FCSTD DOCUMENT  (FreeCAD 1.0R39109 (Git))
Label: asm_roof
License: All rights reserved
LicenseURL: https://en.wikipedia.org/wiki/All_rights_reserved
objects: App::Link×20, App::FeaturePython×15, Assembly::AssemblyLink×2, Assembly::JointGroup×1, Assembly::AssemblyObject×1
EXTERNAL_REF file=../parts/plate_roof.FCStd obj=Body
EXTERNAL_REF file=../secondary/linear_slide.FCStd obj=Body
EXTERNAL_REF file=asm_cam_holder.FCStd obj=Assembly
EXTERNAL_REF file=asm_shf.FCStd obj=Assembly
EXTERNAL_REF file=asm_shf.FCStd obj=SHF12
EXTERNAL_REF file=asm_shf.FCStd obj=Hex_socket_head_cap_screw_DIN_912_M4_15_0
EXTERNAL_REF file=asm_shf.FCStd obj=Hex_socket_head_cap_screw_DIN_912_M5_15_0
EXTERNAL_REF file=asm_shf.FCStd obj=Hex_socket_head_cap_screw_DIN_912_M5_15_001
EXTERNAL_REF file=../secondary/nuts_hexagonal.FCStd obj=Part__Feature001
EXTERNAL_REF file=../secondary/nuts_hexagonal.FCStd obj=Part__Feature

FEATURE [App::Link] plate_roof001  label="plate_roof"
  LinkedObject = -> <external ../parts/plate_roof.FCStd>#Body
FEATURE [App::FeaturePython] GroundedJoint  # Assembly grounded joint (typed FeaturePython)
  ObjectToGround = -> plate_roof001
FEATURE [App::Link] linear_slide  label="linear_slide_12"
  LinkPlacement = pos=(-38,-53.8,-15.1359) rot=(0,0,1;0rad)
  LinkedObject = -> <external ../secondary/linear_slide.FCStd>#Body
  Placement = pos=(-38,-53.8,-15.1359) rot=(0,0,1;0rad)
FEATURE [App::Link] linear_slide001  label="linear_slide_12_001"
  LinkPlacement = pos=(38,-53.8,-15.136) rot=(0,0,1;0rad)
  LinkedObject = -> <external ../secondary/linear_slide.FCStd>#Body
  Placement = pos=(38,-53.8,-15.136) rot=(0,0,1;0rad)
FEATURE [App::Link] asm_cam_holder
  LinkPlacement = pos=(-1.51e-14,-53.8,66.8641) rot=(0,0,1;1.5708rad)
  LinkedObject = -> <external asm_cam_holder.FCStd>#Assembly
  Placement = pos=(-1.51e-14,-53.8,66.8641) rot=(0,0,1;1.5708rad)
FEATURE [App::Link] SHF12
  LinkedObject = -> <external asm_shf.FCStd>#SHF12
FEATURE [App::Link] Hex_socket_head_cap_screw_DIN_912_M4_15_0  label="Hex socket head cap screw DIN 912 M4 15.0"
  LinkPlacement = pos=(12.25,6.5,11.5) rot=(0,-1,0;1.5708rad)
  LinkedObject = -> <external asm_shf.FCStd>#Hex_socket_head_cap_screw_DIN_912_M4_15_0
  Placement = pos=(12.25,6.5,11.5) rot=(0,-1,0;1.5708rad)
FEATURE [App::Link] Hex_socket_head_cap_screw_DIN_912_M5_15_0  label="Hex socket head cap screw DIN 912 M5 15.0"
  LinkPlacement = pos=(18,11,1.16e-14) rot=(0.57735,-0.57735,0.57735;2.0944rad)
  LinkedObject = -> <external asm_shf.FCStd>#Hex_socket_head_cap_screw_DIN_912_M5_15_0
  Placement = pos=(18,11,1.16e-14) rot=(0.57735,-0.57735,0.57735;2.0944rad)
FEATURE [App::Link] Hex_socket_head_cap_screw_DIN_912_M5_15_001  label="Hex socket head cap screw DIN 912 M5 15.001"
  LinkPlacement = pos=(-18,11,1.16e-14) rot=(0.57735,-0.57735,0.57735;2.0944rad)
  LinkedObject = -> <external asm_shf.FCStd>#Hex_socket_head_cap_screw_DIN_912_M5_15_001
  Placement = pos=(-18,11,1.16e-14) rot=(0.57735,-0.57735,0.57735;2.0944rad)
FEATURE [Assembly::AssemblyLink] asm_SHF
  Group = -> [SHF12,Hex_socket_head_cap_screw_DIN_912_M4_15_0,Hex_socket_head_cap_screw_DIN_912_M5_15_0,Hex_socket_head_cap_screw_DIN_912_M5_15_001]
  LinkedObject = -> <external asm_shf.FCStd>#Assembly
  Origin = -> Origin001
  Placement = pos=(38,-53.8,0) rot=(0.57735,0.57735,-0.57735;4.18879rad)
  Rigid = true
FEATURE [App::Link] SHF013
  LinkedObject = -> <external asm_shf.FCStd>#SHF12
FEATURE [App::Link] Hex_socket_head_cap_screw_DIN_912_M4_15_001  label="Hex socket head cap screw DIN 912 M4 15.001"
  LinkPlacement = pos=(12.25,6.5,11.5) rot=(0,-1,0;1.5708rad)
  LinkedObject = -> <external asm_shf.FCStd>#Hex_socket_head_cap_screw_DIN_912_M4_15_0
  Placement = pos=(12.25,6.5,11.5) rot=(0,-1,0;1.5708rad)
FEATURE [App::Link] Hex_socket_head_cap_screw_DIN_912_M5_15_002  label="Hex socket head cap screw DIN 912 M5 15.002"
  LinkPlacement = pos=(18,11,1.16e-14) rot=(0.57735,-0.57735,0.57735;2.0944rad)
  LinkedObject = -> <external asm_shf.FCStd>#Hex_socket_head_cap_screw_DIN_912_M5_15_0
  Placement = pos=(18,11,1.16e-14) rot=(0.57735,-0.57735,0.57735;2.0944rad)
FEATURE [App::Link] Hex_socket_head_cap_screw_DIN_912_M5_15_003  label="Hex socket head cap screw DIN 912 M5 15.003"
  LinkPlacement = pos=(-18,11,1.16e-14) rot=(0.57735,-0.57735,0.57735;2.0944rad)
  LinkedObject = -> <external asm_shf.FCStd>#Hex_socket_head_cap_screw_DIN_912_M5_15_001
  Placement = pos=(-18,11,1.16e-14) rot=(0.57735,-0.57735,0.57735;2.0944rad)
FEATURE [Assembly::AssemblyLink] asm_SHF001
  Group = -> [SHF013,Hex_socket_head_cap_screw_DIN_912_M4_15_001,Hex_socket_head_cap_screw_DIN_912_M5_15_002,Hex_socket_head_cap_screw_DIN_912_M5_15_003]
  LinkedObject = -> <external asm_shf.FCStd>#Assembly
  Origin = -> Origin002
  Placement = pos=(-38,-53.8,0) rot=(0.57735,0.57735,-0.57735;4.18879rad)
  Rigid = true
FEATURE [App::FeaturePython] Joint  label="Fixed"  # Assembly joint (typed FeaturePython)
  Activated = true
  AngleMax = 0
  AngleMin = 0
  Detach1 = false
  Detach2 = false
  Distance = 0
  Distance2 = 0
  EnableAngleMax = false
  EnableAngleMin = false
  EnableLengthMax = false
  EnableLengthMin = false
  JointType = 0 (Fixed)
  LengthMax = 0
  LengthMin = 0
  Placement1 = pos=(18,0,1.16e-14) rot=(-0.57735,0.57735,0.57735;2.0944rad)
  Placement2 = pos=(38,-35.8,0) rot=(0,0,1;0rad)
  Reference1 = -> Assembly [asm_SHF.SHF12.Edge23,asm_SHF.SHF12.Edge23]
  Reference2 = -> Assembly [plate_roof001.Edge35,plate_roof001.Edge35]
FEATURE [App::FeaturePython] Joint001  label="Fixed001"  # Assembly joint (typed FeaturePython)
  Activated = true
  AngleMax = 0
  AngleMin = 0
  Detach1 = false
  Detach2 = false
  Distance = 0
  Distance2 = 0
  EnableAngleMax = false
  EnableAngleMin = false
  EnableLengthMax = false
  EnableLengthMin = false
  JointType = 0 (Fixed)
  LengthMax = 0
  LengthMin = 0
  Placement1 = pos=(18,0,1.16e-14) rot=(-0.57735,0.57735,0.57735;2.0944rad)
  Placement2 = pos=(-38,-35.8,0) rot=(0,0,1;0rad)
  Reference1 = -> Assembly [asm_SHF001.SHF013.Edge23,asm_SHF001.SHF013.Edge23]
  Reference2 = -> Assembly [plate_roof001.Edge41,plate_roof001.Edge41]
FEATURE [App::FeaturePython] Joint002  label="Slider"  # Assembly joint (typed FeaturePython)
  Activated = true
  AngleMax = 0
  AngleMin = 0
  Detach1 = false
  Detach2 = false
  Distance = 0
  Distance2 = 0
  EnableAngleMax = false
  EnableAngleMin = false
  EnableLengthMax = false
  EnableLengthMin = true
  JointType = 3 (Slider)
  LengthMax = 38.1914
  LengthMin = 2.13595
  Placement2 = pos=(0,13,0) rot=(-0.57735,-0.57735,0.57735;4.18879rad)
  Reference1 = -> Assembly [linear_slide001.Edge2,linear_slide001.Edge2]
  Reference2 = -> Assembly [asm_SHF.SHF12.Edge3,asm_SHF.SHF12.Edge3]
FEATURE [App::FeaturePython] Joint003  label="Slider001"  # Assembly joint (typed FeaturePython)
  Activated = true
  AngleMax = 0
  AngleMin = 0
  Detach1 = false
  Detach2 = false
  Distance = 0
  Distance2 = 0
  EnableAngleMax = false
  EnableAngleMin = false
  EnableLengthMax = false
  EnableLengthMin = false
  JointType = 3 (Slider)
  LengthMax = 0
  LengthMin = 0
  Placement2 = pos=(0,13,0) rot=(-0.57735,-0.57735,0.57735;4.18879rad)
  Reference1 = -> Assembly [linear_slide.Edge2,linear_slide.Edge2]
  Reference2 = -> Assembly [asm_SHF001.SHF013.Edge3,asm_SHF001.SHF013.Edge3]
FEATURE [App::FeaturePython] Joint004  label="Fixed002"  # Assembly joint (typed FeaturePython)
  Activated = true
  AngleMax = 0
  AngleMin = 0
  Detach1 = false
  Detach2 = false
  Distance = 0
  Distance2 = 0
  EnableAngleMax = false
  EnableAngleMin = false
  EnableLengthMax = false
  EnableLengthMin = false
  JointType = 0 (Fixed)
  LengthMax = 0
  LengthMin = 0
  Offset2 = pos=(0,0,0) rot=(0,0,1;3.14159rad)
  Placement1 = pos=(0,13,0) rot=(-0.57735,-0.57735,0.57735;4.18879rad)
  Placement2 = pos=(0,0,100) rot=(0,0,1;3.14159rad)
  Reference1 = -> Assembly [asm_cam_holder.asm_SHF001.SHF013.Edge3,asm_cam_holder.asm_SHF001.SHF013.Edge3]
  Reference2 = -> Assembly [linear_slide001.Edge3,linear_slide001.Edge3]
FEATURE [App::FeaturePython] Joint005  label="Fixed003"  # Assembly joint (typed FeaturePython)
  Activated = true
  AngleMax = 0
  AngleMin = 0
  Detach1 = false
  Detach2 = false
  Distance = 0
  Distance2 = 0
  EnableAngleMax = false
  EnableAngleMin = false
  EnableLengthMax = false
  EnableLengthMin = false
  JointType = 0 (Fixed)
  LengthMax = 0
  LengthMin = 0
  Placement1 = pos=(0,0,100) rot=(0,0,1;0rad)
  Placement2 = pos=(0,13,0) rot=(-0.57735,-0.57735,0.57735;4.18879rad)
  Reference1 = -> Assembly [linear_slide.Edge3,linear_slide.Edge3]
  Reference2 = -> Assembly [asm_cam_holder.asm_SHF.SHF12.Edge3,asm_cam_holder.asm_SHF.SHF12.Edge3]
FEATURE [App::Link] Hexagonal_Nut_M5_CBALN5  label="Hexagonal Nut M5_CBALN5"
  LinkPlacement = pos=(-38,-71.8,66.8641) rot=(0,1,0;4.71239rad)
  LinkedObject = -> <external ../secondary/nuts_hexagonal.FCStd>#Part__Feature001
  Placement = pos=(-38,-71.8,66.8641) rot=(0,1,0;4.71239rad)
FEATURE [App::Link] Hexagonal_Nut_M5_CBALN006  label="Hexagonal Nut M5_CBALN006"
  LinkPlacement = pos=(38,-71.8,66.864) rot=(0.707107,0,0.707107;3.14159rad)
  LinkedObject = -> <external ../secondary/nuts_hexagonal.FCStd>#Part__Feature001
  Placement = pos=(38,-71.8,66.864) rot=(0.707107,0,0.707107;3.14159rad)
FEATURE [App::Link] Hexagonal_Nut_M5_CBALN007  label="Hexagonal Nut M5_CBALN007"
  LinkPlacement = pos=(-38,-35.8,66.8641) rot=(0,-1,0;1.5708rad)
  LinkedObject = -> <external ../secondary/nuts_hexagonal.FCStd>#Part__Feature001
  Placement = pos=(-38,-35.8,66.8641) rot=(0,-1,0;1.5708rad)
FEATURE [App::Link] Hexagonal_Nut_M5_CBALN008  label="Hexagonal Nut M5_CBALN008"
  LinkPlacement = pos=(38,-35.8,66.864) rot=(0.707107,0,0.707107;3.14159rad)
  LinkedObject = -> <external ../secondary/nuts_hexagonal.FCStd>#Part__Feature001
  Placement = pos=(38,-35.8,66.864) rot=(0.707107,0,0.707107;3.14159rad)
FEATURE [App::FeaturePython] Joint006  label="Fixed004"  # Assembly joint (typed FeaturePython)
  Activated = true
  AngleMax = 0
  AngleMin = 0
  Detach1 = false
  Detach2 = false
  Distance = 0
  Distance2 = 0
  EnableAngleMax = false
  EnableAngleMin = false
  EnableLengthMax = false
  EnableLengthMin = false
  JointType = 0 (Fixed)
  LengthMax = 0
  LengthMin = 0
  Offset2 = pos=(0,0,-11) rot=(0,0,1;0rad)
  Placement1 = pos=(0,0,0) rot=(0,-1,0;1.5708rad)
  Placement2 = pos=(-1.8e-15,-7e-15,16) rot=(0,0,1;0rad)
  Reference1 = -> Assembly [Hexagonal_Nut_M5_CBALN008.Edge48,Hexagonal_Nut_M5_CBALN008.Edge48]
  Reference2 = -> Assembly [asm_cam_holder.asm_SHF001.Hex_socket_head_cap_screw_DIN_912_M5_15_002.Edge11,asm_cam_holder.asm_SHF001.Hex_socket_head_cap_screw_DIN_912_M5_15_002.Edge11]
FEATURE [App::FeaturePython] Joint007  label="Fixed005"  # Assembly joint (typed FeaturePython)
  Activated = true
  AngleMax = 0
  AngleMin = 0
  Detach1 = false
  Detach2 = false
  Distance = 0
  Distance2 = 0
  EnableAngleMax = false
  EnableAngleMin = false
  EnableLengthMax = false
  EnableLengthMin = false
  JointType = 0 (Fixed)
  LengthMax = 0
  LengthMin = 0
  Offset2 = pos=(0,0,-11) rot=(0,0,1;0rad)
  Placement1 = pos=(0,0,0) rot=(0,-1,0;1.5708rad)
  Placement2 = pos=(0,-3.6e-15,16) rot=(0,0,1;0rad)
  Reference1 = -> Assembly [Hexagonal_Nut_M5_CBALN006.Edge28,Hexagonal_Nut_M5_CBALN006.Edge28]
  Reference2 = -> Assembly [asm_cam_holder.asm_SHF001.Hex_socket_head_cap_screw_DIN_912_M5_15_003.Edge11,asm_cam_holder.asm_SHF001.Hex_socket_head_cap_screw_DIN_912_M5_15_003.Edge11]
FEATURE [App::FeaturePython] Joint008  label="Fixed006"  # Assembly joint (typed FeaturePython)
  Activated = true
  AngleMax = 0
  AngleMin = 0
  Detach1 = false
  Detach2 = false
  Distance = 0
  Distance2 = 0
  EnableAngleMax = false
  EnableAngleMin = false
  EnableLengthMax = false
  EnableLengthMin = false
  JointType = 0 (Fixed)
  LengthMax = 0
  LengthMin = 0
  Offset2 = pos=(0,0,-11) rot=(0,0,1;0rad)
  Placement1 = pos=(0,0,0) rot=(0,1,0;4.71239rad)
  Placement2 = pos=(0,-3.6e-15,16) rot=(0,0,1;0rad)
  Reference1 = -> Assembly [Hexagonal_Nut_M5_CBALN007.Edge28,Hexagonal_Nut_M5_CBALN007.Edge28]
  Reference2 = -> Assembly [asm_cam_holder.asm_SHF.Hex_socket_head_cap_screw_DIN_912_M5_15_001.Edge11,asm_cam_holder.asm_SHF.Hex_socket_head_cap_screw_DIN_912_M5_15_001.Edge11]
FEATURE [App::FeaturePython] Joint009  label="Fixed007"  # Assembly joint (typed FeaturePython)
  Activated = true
  AngleMax = 0
  AngleMin = 0
  Detach1 = false
  Detach2 = false
  Distance = 0
  Distance2 = 0
  EnableAngleMax = false
  EnableAngleMin = false
  EnableLengthMax = false
  EnableLengthMin = false
  JointType = 0 (Fixed)
  LengthMax = 0
  LengthMin = 0
  Offset2 = pos=(0,0,-11) rot=(0,0,1;0rad)
  Placement1 = pos=(0,0,0) rot=(0,-1,0;1.5708rad)
  Placement2 = pos=(-1.8e-15,-7e-15,16) rot=(0,0,1;0rad)
  Reference1 = -> Assembly [Hexagonal_Nut_M5_CBALN5.Edge28,Hexagonal_Nut_M5_CBALN5.Edge28]
  Reference2 = -> Assembly [asm_cam_holder.asm_SHF.Hex_socket_head_cap_screw_DIN_912_M5_15_0.Edge11,asm_cam_holder.asm_SHF.Hex_socket_head_cap_screw_DIN_912_M5_15_0.Edge11]
FEATURE [App::Link] Hexagonal_Nut_M4_CBALN4  label="Hexagonal Nut M4_CBALN4"
  LinkPlacement = pos=(32.96,-17.7689,66.8641) rot=(0.707107,0,0.707107;3.14159rad)
  LinkedObject = -> <external ../secondary/nuts_hexagonal.FCStd>#Part__Feature
  Placement = pos=(32.96,-17.7689,66.8641) rot=(0.707107,0,0.707107;3.14159rad)
FEATURE [App::Link] Hexagonal_Nut_M4_CBALN005  label="Hexagonal Nut M4_CBALN005"
  LinkPlacement = pos=(-32.96,-17.7689,66.8641) rot=(0.707107,0,0.707107;3.14159rad)
  LinkedObject = -> <external ../secondary/nuts_hexagonal.FCStd>#Part__Feature
  Placement = pos=(-32.96,-17.7689,66.8641) rot=(0.707107,0,0.707107;3.14159rad)
FEATURE [App::Link] Hexagonal_Nut_M4_CBALN006  label="Hexagonal Nut M4_CBALN006"
  LinkPlacement = pos=(-32.96,20.2311,66.8641) rot=(0.707107,0,0.707107;3.14159rad)
  LinkedObject = -> <external ../secondary/nuts_hexagonal.FCStd>#Part__Feature
  Placement = pos=(-32.96,20.2311,66.8641) rot=(0.707107,0,0.707107;3.14159rad)
FEATURE [App::Link] Hexagonal_Nut_M4_CBALN007  label="Hexagonal Nut M4_CBALN007"
  LinkPlacement = pos=(32.96,20.2311,66.864) rot=(0.707107,0,0.707107;3.14159rad)
  LinkedObject = -> <external ../secondary/nuts_hexagonal.FCStd>#Part__Feature
  Placement = pos=(32.96,20.2311,66.864) rot=(0.707107,0,0.707107;3.14159rad)
FEATURE [App::FeaturePython] Joint010  label="Fixed008"  # Assembly joint (typed FeaturePython)
  Activated = true
  AngleMax = 0
  AngleMin = 0
  Detach1 = false
  Detach2 = false
  Distance = 0
  Distance2 = 0
  EnableAngleMax = false
  EnableAngleMin = false
  EnableLengthMax = false
  EnableLengthMin = false
  JointType = 0 (Fixed)
  LengthMax = 0
  LengthMin = 0
  Offset2 = pos=(0,0,3) rot=(0,0,1;0rad)
  Placement1 = pos=(0,0,0) rot=(0,-1,0;1.5708rad)
  Placement2 = pos=(-6.98683,35.5575,3) rot=(0,0,1;0rad)
  Reference1 = -> Assembly [Hexagonal_Nut_M4_CBALN007.Edge31,Hexagonal_Nut_M4_CBALN007.Edge31]
  Reference2 = -> Assembly [asm_cam_holder.asm_cam_mount.Hex_screw_M4_10_003.Edge2,asm_cam_holder.asm_cam_mount.Hex_screw_M4_10_003.Edge2]
FEATURE [App::FeaturePython] Joint011  label="Fixed009"  # Assembly joint (typed FeaturePython)
  Activated = true
  AngleMax = 0
  AngleMin = 0
  Detach1 = false
  Detach2 = false
  Distance = 0
  Distance2 = 0
  EnableAngleMax = false
  EnableAngleMin = false
  EnableLengthMax = false
  EnableLengthMin = false
  JointType = 0 (Fixed)
  LengthMax = 0
  LengthMin = 0
  Offset2 = pos=(0,0,3) rot=(0,0,1;0rad)
  Placement1 = pos=(0,0,0) rot=(0,-1,0;1.5708rad)
  Placement2 = pos=(-6.98683,35.5575,3) rot=(0,0,1;0rad)
  Reference1 = -> Assembly [Hexagonal_Nut_M4_CBALN006.Edge31,Hexagonal_Nut_M4_CBALN006.Edge31]
  Reference2 = -> Assembly [asm_cam_holder.asm_cam_mount.Hex_screw_M4_10_001.Edge2,asm_cam_holder.asm_cam_mount.Hex_screw_M4_10_001.Edge2]
FEATURE [App::FeaturePython] Joint012  label="Fixed010"  # Assembly joint (typed FeaturePython)
  Activated = true
  AngleMax = 0
  AngleMin = 0
  Detach1 = false
  Detach2 = false
  Distance = 0
  Distance2 = 0
  EnableAngleMax = false
  EnableAngleMin = false
  EnableLengthMax = false
  EnableLengthMin = false
  JointType = 0 (Fixed)
  LengthMax = 0
  LengthMin = 0
  Offset2 = pos=(0,0,3) rot=(0,0,1;0rad)
  Placement1 = pos=(0,0,0) rot=(0,-1,0;1.5708rad)
  Placement2 = pos=(-6.98683,35.5575,3) rot=(0,0,1;0rad)
  Reference1 = -> Assembly [Hexagonal_Nut_M4_CBALN005.Edge31,Hexagonal_Nut_M4_CBALN005.Edge31]
  Reference2 = -> Assembly [asm_cam_holder.asm_cam_mount.Hex_screw_M4_10_0.Edge2,asm_cam_holder.asm_cam_mount.Hex_screw_M4_10_0.Edge2]
FEATURE [App::FeaturePython] Joint013  label="Fixed011"  # Assembly joint (typed FeaturePython)
  Activated = true
  AngleMax = 0
  AngleMin = 0
  Detach1 = false
  Detach2 = false
  Distance = 0
  Distance2 = 0
  EnableAngleMax = false
  EnableAngleMin = false
  EnableLengthMax = false
  EnableLengthMin = false
  JointType = 0 (Fixed)
  LengthMax = 0
  LengthMin = 0
  Offset2 = pos=(0,0,3) rot=(0,0,1;0rad)
  Placement1 = pos=(0,0,0) rot=(0,-1,0;1.5708rad)
  Placement2 = pos=(-6.98683,35.5575,3) rot=(0,0,1;0rad)
  Reference1 = -> Assembly [Hexagonal_Nut_M4_CBALN4.Edge31,Hexagonal_Nut_M4_CBALN4.Edge31]
  Reference2 = -> Assembly [asm_cam_holder.asm_cam_mount.Hex_screw_M4_10_002.Edge2,asm_cam_holder.asm_cam_mount.Hex_screw_M4_10_002.Edge2]
FEATURE [Assembly::JointGroup] Joints
  Group = -> [GroundedJoint,Joint,Joint001,Joint002,Joint003,Joint004,Joint005,Joint006,Joint007,Joint008,Joint009,Joint010,Joint011,Joint012,Joint013]
FEATURE [Assembly::AssemblyObject] Assembly  label="asm_roof"
  Group = -> [Joints,plate_roof001,GroundedJoint,linear_slide,linear_slide001,asm_cam_holder,asm_SHF,asm_SHF001,Joint,Joint001,Joint002,Joint003,Joint004,Joint005,Hexagonal_Nut_M5_CBALN5,Hexagonal_Nut_M5_CBALN006,Hexagonal_Nut_M5_CBALN007,Hexagonal_Nut_M5_CBALN008,Joint006,Joint007,Joint008,Joint009,Hexagonal_Nut_M4_CBALN4,Hexagonal_Nut_M4_CBALN005,Hexagonal_Nut_M4_CBALN006,Hexagonal_Nut_M4_CBALN007,Joint010,+3 more]
  Origin = -> Origin
  Type = Assembly

RESOLVED EXTERNAL PARTS (link-assembly join: the EXTERNAL_REF files above that resolve inside this repo's crawl, each included once):
---- part ../parts/plate_roof.FCStd = doc fcstd_1de5e0d9f138 ----
FCSTD DOCUMENT  (FreeCAD 1.0R38641 +468 (Git))
Label: plate_roof
License: All rights reserved
LicenseURL: https://en.wikipedia.org/wiki/All_rights_reserved
objects: TechDraw::DrawViewDimension×10, TechDraw::DrawProjGroupItem×2, Sketcher::SketchObject×1, PartDesign::Pad×1, PartDesign::Body×1, TechDraw::DrawSVGTemplate×1, TechDraw::DrawProjGroup×1, TechDraw::DrawPage×1
note: 22 computed .brp shape members not serialized (recipe doc carries the construction recipe); baked Part::Feature solids carry a one-line shape summary decoded from their .brp

FEATURE [Sketcher::SketchObject] Sketch
  ArcFitTolerance = 1e-06
  AttachmentSupport = -> [XY_Plane]
  FullyConstrained = false
  MakeInternals = false
  MapMode = 5
  sketch-geometry (16):
    g0: LineSegment StartX=-100 StartY=200 StartZ=0 EndX=-100 EndY=-200 EndZ=0
    g1: LineSegment StartX=-100 StartY=-200 StartZ=0 EndX=100 EndY=-200 EndZ=0
    g2: LineSegment StartX=100 StartY=-200 StartZ=0 EndX=100 EndY=200 EndZ=0
    g3: LineSegment StartX=100 StartY=200 StartZ=0 EndX=-100 EndY=200 EndZ=0
    g4: Circle CenterX=-44 CenterY=50.2 CenterZ=0 NormalX=0 NormalY=0 NormalZ=1 AngleXU=0 Radius=2.45
    g5: Circle CenterX=-44 CenterY=-157.8 CenterZ=0 NormalX=0 NormalY=0 NormalZ=1 AngleXU=0 Radius=2.45
    g6: Circle CenterX=44 CenterY=50.2 CenterZ=0 NormalX=0 NormalY=0 NormalZ=1 AngleXU=0 Radius=2.45
    g7: Circle CenterX=44 CenterY=-157.8 CenterZ=0 NormalX=0 NormalY=0 NormalZ=1 AngleXU=0 Radius=2.45
    g8: Circle [constr] CenterX=0 CenterY=0 CenterZ=0 NormalX=0 NormalY=0 NormalZ=1 AngleXU=0 Radius=9.44112
    g9: Circle CenterX=-38 CenterY=-35.8 CenterZ=0 NormalX=0 NormalY=0 NormalZ=1 AngleXU=0 Radius=1.95
    g10: Circle CenterX=-38 CenterY=-71.8 CenterZ=0 NormalX=0 NormalY=0 NormalZ=1 AngleXU=0 Radius=1.95
    g11: Circle CenterX=-38 CenterY=-53.8 CenterZ=0 NormalX=0 NormalY=0 NormalZ=1 AngleXU=0 Radius=6.5
    g12: Circle CenterX=38 CenterY=-35.8 CenterZ=0 NormalX=0 NormalY=0 NormalZ=1 AngleXU=0 Radius=1.95
    g13: Circle CenterX=38 CenterY=-53.8 CenterZ=0 NormalX=0 NormalY=0 NormalZ=1 AngleXU=0 Radius=6.5
    g14: Circle CenterX=38 CenterY=-71.8 CenterZ=0 NormalX=0 NormalY=0 NormalZ=1 AngleXU=0 Radius=1.95
    g15: LineSegment [constr] StartX=0 StartY=0 StartZ=0 EndX=0 EndY=174.663 EndZ=0
  constraints (44):
    c: Coincident(g0,g1)
    c: Coincident(g1,g2)
    c: Coincident(g2,g3)
    c: Coincident(g3,g0)
    c: Vertical(g0)
    c: Vertical(g2)
    c: Horizontal(g1)
    c: Horizontal(g3)
    c: DistanceY(g0,g0) = 400
    c: DistanceX(g3,g3) = 200
    c: Vertical(g4,g5)
    c: Diameter(g4) = 4.9
    c: Equal(g4,g5)
    c: DistanceY(g5,g4) = 208
    c: Horizontal(g6,g4)
    c: Horizontal(g7,g5)
    c: Equal(g6,g4)
    c: Equal(g4,g7)
    c: DistanceX(g4,g6) = 88
    c: Vertical(g7,g6)
    c: DistanceY(g8,g4) = 50.2
    c: DistanceX(g4,g8) = 44
    c: Distance(g8,g3) = 200
    c: Distance(g8,g0) = 100
    c: Vertical(g9,g11)
    c: Vertical(g11,g10)
    c: Vertical(g12,g13)
    c: Vertical(g13,g14)
    c: DistanceY(g11,g9) = 18
    c: DistanceY(g10,g11) = 18
    c: Diameter(g9) = 3.9
    c: Equal(g9,g10)
    c: Equal(g10,g12)
    c: Equal(g12,g14)
    c: Horizontal(g9,g12)
    c: Horizontal(g10,g14)
    c: Equal(g11,g13)
    c: Diameter(g11) = 13
    c: DistanceX(g11,g8) = 38
    c: Horizontal(g11,g13)
    c: DistanceY(g11,g4) = 104
    c: Coincident(g15,g8)
    c: Symmetric(g11,g13,g15)
    c: Coincident(g8,g-1)
FEATURE [PartDesign::Pad] Pad
  Direction = (0,0,1)
  Length = 3
  Length2 = 10
  Profile = -> Sketch
  ReferenceAxis = -> Sketch [N_Axis]
  Refine = true
  Suppressed = false
  Type = 0
FEATURE [PartDesign::Body] Body  label="plate_roof"
  AllowCompound = false
  Group = -> [Sketch,Pad]
  Origin = -> Origin
  Tip = -> Pad
FEATURE [TechDraw::DrawSVGTemplate] Template
  EditableTexts = approval_person=B. Hecate; creator=Djordje Vujic; date_of_issue=20.1.25.; document_type=Assembly Drawing; general_tolerances=ISO 2768-m; identification_number=DN; language_code=EN; part_material=Stainless steel Mat.No. 1.4301; revision_index=AAA; sheet_number=1 / 3; sheet_scale=1 : 2; title=plate_roof
  Height = 297
  Orientation = 0
  Template = /snap/freecad/1248/usr/share/Mod/TechDraw/Templates/A4_Portrait_ISO5457_minimal.svg
  Width = 210
FEATURE [TechDraw::DrawProjGroupItem] ProjItem  label="Front"
  CoarseView = false
  Direction = (0,0,1)
  Focus = 100
  HardHidden = false
  IsoCount = 0
  IsoHidden = false
  IsoVisible = false
  LockPosition = true
  Perspective = false
  Rotation = 0
  RotationVector = (1,0,0)
  Scale = 0.5
  ScaleType = 0
  ScrubCount = 1
  SeamHidden = false
  SeamVisible = false
  SmoothHidden = false
  SmoothVisible = true
  Source = -> [Body]
  Type = 0
  X = 0
  XDirection = (1,0,0)
  Y = 0
FEATURE [TechDraw::DrawProjGroupItem] ProjItem001  label="Bottom"
  CoarseView = false
  Direction = (0,-1,0)
  Focus = 100
  HardHidden = false
  IsoCount = 0
  IsoHidden = false
  IsoVisible = false
  LockPosition = false
  Perspective = false
  Rotation = 0
  RotationVector = (1,0,0)
  Scale = 0.5
  ScaleType = 0
  ScrubCount = 1
  SeamHidden = false
  SeamVisible = false
  SmoothHidden = false
  SmoothVisible = true
  Source = -> [Body]
  Type = 5
  X = 0
  XDirection = (1,0,0)
  Y = 115.75
FEATURE [TechDraw::DrawProjGroup] ProjGroup
  Anchor = -> ProjItem
  AutoDistribute = true
  LockPosition = false
  ProjectionType = 0
  Rotation = 0
  Scale = 0.5
  ScaleType = 2
  Source = -> [Body]
  Views = -> [ProjItem,ProjItem001]
  X = 105
  Y = 162.983
  spacingX = 15
  spacingY = 15
FEATURE [TechDraw::DrawViewDimension] Dimension
  AngleOverride = false
  Arbitrary = false
  ArbitraryTolerances = false
  BoxCorners = (2) [(-50,-0.75,0),(50,0.75,0)]
  EqualTolerance = true
  ExtensionAngle = 0
  FormatSpec = %.2w
  FormatSpecOverTolerance = %+.2w
  FormatSpecUnderTolerance = %+.2w
  Inverted = false
  LineAngle = 0
  LockPosition = false
  MeasureType = 1
  OverTolerance = 0
  References2D = -> [ProjItem001]
  Rotation = 0
  ScaleType = 0
  TheoreticalExact = false
  Type = 2
  UnderTolerance = 0
  X = -62.2509
  Y = -6.95305
FEATURE [TechDraw::DrawViewDimension] Dimension001
  AngleOverride = false
  Arbitrary = false
  ArbitraryTolerances = false
  BoxCorners = (2) [(-50,-0.75,0),(50,0.75,0)]
  EqualTolerance = true
  ExtensionAngle = 0
  FormatSpec = %.2w
  FormatSpecOverTolerance = %+.2w
  FormatSpecUnderTolerance = %+.2w
  Inverted = false
  LineAngle = 0
  LockPosition = false
  MeasureType = 1
  OverTolerance = 0
  References2D = -> [ProjItem001]
  Rotation = 0
  ScaleType = 0
  TheoreticalExact = false
  Type = 1
  UnderTolerance = 0
  X = 0
  Y = -5.41651
FEATURE [TechDraw::DrawViewDimension] Dimension002
  AngleOverride = false
  Arbitrary = false
  ArbitraryTolerances = false
  BoxCorners = (2) [(-50,-100,0),(50,100,0)]
  EqualTolerance = true
  ExtensionAngle = 0
  FormatSpec = %.2w
  FormatSpecOverTolerance = %+.2w
  FormatSpecUnderTolerance = %+.2w
  Inverted = false
  LineAngle = 0
  LockPosition = false
  MeasureType = 1
  OverTolerance = 0
  References2D = -> [ProjItem]
  Rotation = 0
  ScaleType = 0
  TheoreticalExact = false
  Type = 2
  UnderTolerance = 0
  X = -64.6458
  Y = 3.29053
FEATURE [TechDraw::DrawViewDimension] Dimension003
  AngleOverride = false
  Arbitrary = false
  ArbitraryTolerances = false
  BoxCorners = (2) [(-50,-100,0),(50,100,0)]
  EqualTolerance = true
  ExtensionAngle = 0
  FormatSpec = %.2w
  FormatSpecOverTolerance = %+.2w
  FormatSpecUnderTolerance = %+.2w
  Inverted = false
  LineAngle = 0
  LockPosition = false
  MeasureType = 1
  OverTolerance = 0
  References2D = -> [ProjItem]
  Rotation = 0
  ScaleType = 0
  TheoreticalExact = false
  Type = 0
  UnderTolerance = 0
  X = 29.0917
  Y = -31.4
FEATURE [TechDraw::DrawViewDimension] Dimension004
  AngleOverride = false
  Arbitrary = false
  ArbitraryTolerances = false
  BoxCorners = (2) [(-50,-100,0),(50,100,0)]
  EqualTolerance = true
  ExtensionAngle = 0
  FormatSpec = %.2w
  FormatSpecOverTolerance = %+.2w
  FormatSpecUnderTolerance = %+.2w
  Inverted = false
  LineAngle = 0
  LockPosition = false
  MeasureType = 1
  OverTolerance = 0
  References2D = -> [ProjItem]
  Rotation = 0
  ScaleType = 0
  TheoreticalExact = false
  Type = 0
  UnderTolerance = 0
  X = 0
  Y = -5.52183
FEATURE [TechDraw::DrawViewDimension] Dimension005
  AngleOverride = false
  Arbitrary = false
  ArbitraryTolerances = false
  BoxCorners = (2) [(-50,-100,0),(50,100,0)]
  EqualTolerance = true
  ExtensionAngle = 0
  FormatSpec = %.2w
  FormatSpecOverTolerance = %+.2w
  FormatSpecUnderTolerance = %+.2w
  Inverted = false
  LineAngle = 0
  LockPosition = false
  MeasureType = 1
  OverTolerance = 0
  References2D = -> [ProjItem]
  Rotation = 0
  ScaleType = 0
  TheoreticalExact = false
  Type = 0
  UnderTolerance = 0
  X = -34.5
  Y = -5.52183
FEATURE [TechDraw::DrawViewDimension] Dimension006
  AngleOverride = false
  Arbitrary = false
  ArbitraryTolerances = false
  BoxCorners = (2) [(-50,-100,0),(50,100,0)]
  EqualTolerance = true
  ExtensionAngle = 0
  FormatSpec = %.2w
  FormatSpecOverTolerance = %+.2w
  FormatSpecUnderTolerance = %+.2w
  Inverted = false
  LineAngle = 0
  LockPosition = false
  MeasureType = 1
  OverTolerance = 0
  References2D = -> [ProjItem]
  Rotation = 0
  ScaleType = 0
  TheoreticalExact = false
  Type = 0
  UnderTolerance = 0
  X = -33.0527
  Y = -22.4
FEATURE [TechDraw::DrawViewDimension] Dimension007
  AngleOverride = false
  Arbitrary = false
  ArbitraryTolerances = false
  BoxCorners = (2) [(-50,-100,0),(50,100,0)]
  EqualTolerance = false
  ExtensionAngle = 0
  FormatSpec = ⌀%.2w
  FormatSpecOverTolerance = %+.2w
  FormatSpecUnderTolerance = -%.2w
  Inverted = false
  LineAngle = 0
  LockPosition = false
  MeasureType = 1
  OverTolerance = 1
  References2D = -> [ProjItem]
  Rotation = 0
  ScaleType = 0
  TheoreticalExact = false
  Type = 5
  UnderTolerance = 0.9
  X = -9.88409
  Y = -19.3744
FEATURE [TechDraw::DrawViewDimension] Dimension008
  AngleOverride = false
  Arbitrary = false
  ArbitraryTolerances = false
  BoxCorners = (2) [(-50,-100,0),(50,100,0)]
  EqualTolerance = true
  ExtensionAngle = 0
  FormatSpec = %.2w
  FormatSpecOverTolerance = %+.2w
  FormatSpecUnderTolerance = %+.2w
  Inverted = false
  LineAngle = 0
  LockPosition = false
  MeasureType = 1
  OverTolerance = 1
  References2D = -> [ProjItem]
  Rotation = 0
  ScaleType = 0
  TheoreticalExact = false
  Type = 0
  UnderTolerance = -1
  X = 9.62605
  Y = -67.95
FEATURE [TechDraw::DrawViewDimension] Dimension009
  AngleOverride = false
  Arbitrary = false
  ArbitraryTolerances = false
  BoxCorners = (2) [(-50,-100,0),(50,100,0)]
  EqualTolerance = false
  ExtensionAngle = 0
  FormatSpec = ⌀%.2w
  FormatSpecOverTolerance = %+.2w
  FormatSpecUnderTolerance = -%.2w
  Inverted = false
  LineAngle = 0
  LockPosition = false
  MeasureType = 1
  OverTolerance = 0.1
  References2D = -> [ProjItem]
  Rotation = 0
  ScaleType = 0
  TheoreticalExact = false
  Type = 5
  UnderTolerance = 0
  X = -5.75191
  Y = -38.5146
FEATURE [TechDraw::DrawPage] Page
  KeepUpdated = true
  NextBalloonIndex = 1
  ProjectionType = 0
  Template = -> Template
  Views = -> [ProjGroup,Dimension,Dimension001,Dimension002,Dimension003,Dimension004,Dimension005,Dimension006,Dimension007,Dimension008,Dimension009]
---- part ../secondary/linear_slide.FCStd = doc fcstd_3a6566d32c48 ----
FCSTD DOCUMENT  (FreeCAD 1.0R39109 (Git))
Label: linear_slide
License: All rights reserved
LicenseURL: https://en.wikipedia.org/wiki/All_rights_reserved
objects: Sketcher::SketchObject×1, PartDesign::Pad×1, PartDesign::Body×1
note: 6 computed .brp shape members not serialized (recipe doc carries the construction recipe); baked Part::Feature solids carry a one-line shape summary decoded from their .brp

FEATURE [Sketcher::SketchObject] Sketch
  ArcFitTolerance = 1e-06
  AttachmentSupport = -> [XY_Plane]
  FullyConstrained = true
  MakeInternals = false
  MapMode = 5
  sketch-geometry (1):
    g0: Circle CenterX=0 CenterY=0 CenterZ=0 NormalX=0 NormalY=0 NormalZ=1 AngleXU=0 Radius=6
  constraints (2):
    c: Coincident(g0,g-1)
    c: Diameter(g0) = 12
FEATURE [PartDesign::Pad] Pad
  Direction = (0,0,1)
  Length = 100
  Length2 = 10
  Profile = -> Sketch
  ReferenceAxis = -> Sketch [N_Axis]
  Refine = true
  Suppressed = false
  Type = 0
FEATURE [PartDesign::Body] Body  label="linear_slide_12"
  AllowCompound = false
  Group = -> [Sketch,Pad]
  Origin = -> Origin
  Tip = -> Pad
---- part asm_cam_holder.FCStd = doc fcstd_0fa39fadfb01 ----
FCSTD DOCUMENT  (FreeCAD 1.0R39109 (Git))
Label: asm_cam_holder
License: All rights reserved
LicenseURL: https://en.wikipedia.org/wiki/All_rights_reserved
objects: App::Link×24, App::FeaturePython×5, Assembly::AssemblyLink×4, Assembly::JointGroup×1, Assembly::AssemblyObject×1
EXTERNAL_REF file=../parts/cam_holder/cam_holder_plate.FCStd obj=Body
EXTERNAL_REF file=asm_shf.FCStd obj=Assembly
EXTERNAL_REF file=asm_shf.FCStd obj=SHF12
EXTERNAL_REF file=asm_shf.FCStd obj=Hex_socket_head_cap_screw_DIN_912_M4_15_0
EXTERNAL_REF file=asm_shf.FCStd obj=Hex_socket_head_cap_screw_DIN_912_M5_15_0
EXTERNAL_REF file=asm_shf.FCStd obj=Hex_socket_head_cap_screw_DIN_912_M5_15_001
EXTERNAL_REF file=asm_rpi.FCStd obj=Assembly
EXTERNAL_REF file=asm_rpi.FCStd obj=Raspberry_Pi_4_Model_B
EXTERNAL_REF file=asm_rpi.FCStd obj=Hex_screw_M2_5_04_0
EXTERNAL_REF file=asm_rpi.FCStd obj=Hex_screw_M2_5_04_001
EXTERNAL_REF file=asm_rpi.FCStd obj=Hex_screw_M2_5_04_002
EXTERNAL_REF file=asm_rpi.FCStd obj=Hex_screw_M2_5_04_003
EXTERNAL_REF file=asm_cam_mount.FCStd obj=Assembly
EXTERNAL_REF file=asm_cam_mount.FCStd obj=cam_holder_base
EXTERNAL_REF file=asm_cam_mount.FCStd obj=Raspberry_Pi_HQ_Camera_with_cs_mount_lens_v014
EXTERNAL_REF file=asm_cam_mount.FCStd obj=Hex_screw_M2_5_04_0
EXTERNAL_REF file=asm_cam_mount.FCStd obj=Hex_screw_M2_5_04_001
EXTERNAL_REF file=asm_cam_mount.FCStd obj=Hex_screw_M2_5_04_002
EXTERNAL_REF file=asm_cam_mount.FCStd obj=Hex_screw_M2_5_04_003
EXTERNAL_REF file=asm_cam_mount.FCStd obj=Hex_screw_M4_10_0
EXTERNAL_REF file=asm_cam_mount.FCStd obj=Hex_screw_M4_10_001
EXTERNAL_REF file=asm_cam_mount.FCStd obj=Hex_screw_M4_10_002
EXTERNAL_REF file=asm_cam_mount.FCStd obj=Hex_screw_M4_10_003

FEATURE [App::Link] cam_holder_plate
  LinkedObject = -> <external ../parts/cam_holder/cam_holder_plate.FCStd>#Body
FEATURE [App::FeaturePython] GroundedJoint  # Assembly grounded joint (typed FeaturePython)
  ObjectToGround = -> cam_holder_plate
FEATURE [App::Link] SHF12
  LinkedObject = -> <external asm_shf.FCStd>#SHF12
FEATURE [App::Link] Hex_socket_head_cap_screw_DIN_912_M4_15_0  label="Hex socket head cap screw DIN 912 M4 15.0"
  LinkPlacement = pos=(12.25,6.5,11.5) rot=(0,-1,0;1.5708rad)
  LinkedObject = -> <external asm_shf.FCStd>#Hex_socket_head_cap_screw_DIN_912_M4_15_0
  Placement = pos=(12.25,6.5,11.5) rot=(0,-1,0;1.5708rad)
FEATURE [App::Link] Hex_socket_head_cap_screw_DIN_912_M5_15_0  label="Hex socket head cap screw DIN 912 M5 15.0"
  LinkPlacement = pos=(18,11,1.16e-14) rot=(0.57735,-0.57735,0.57735;2.0944rad)
  LinkedObject = -> <external asm_shf.FCStd>#Hex_socket_head_cap_screw_DIN_912_M5_15_0
  Placement = pos=(18,11,1.16e-14) rot=(0.57735,-0.57735,0.57735;2.0944rad)
FEATURE [App::Link] Hex_socket_head_cap_screw_DIN_912_M5_15_001  label="Hex socket head cap screw DIN 912 M5 15.001"
  LinkPlacement = pos=(-18,11,1.16e-14) rot=(0.57735,-0.57735,0.57735;2.0944rad)
  LinkedObject = -> <external asm_shf.FCStd>#Hex_socket_head_cap_screw_DIN_912_M5_15_001
  Placement = pos=(-18,11,1.16e-14) rot=(0.57735,-0.57735,0.57735;2.0944rad)
FEATURE [Assembly::AssemblyLink] asm_SHF
  Group = -> [SHF12,Hex_socket_head_cap_screw_DIN_912_M4_15_0,Hex_socket_head_cap_screw_DIN_912_M5_15_0,Hex_socket_head_cap_screw_DIN_912_M5_15_001]
  LinkedObject = -> <external asm_shf.FCStd>#Assembly
  Origin = -> Origin001
  Placement = pos=(0,38,3) rot=(0,0.707107,0.707107;3.14159rad)
  Rigid = true
FEATURE [App::Link] SHF013
  LinkedObject = -> <external asm_shf.FCStd>#SHF12
FEATURE [App::Link] Hex_socket_head_cap_screw_DIN_912_M4_15_001  label="Hex socket head cap screw DIN 912 M4 15.001"
  LinkPlacement = pos=(12.25,6.5,11.5) rot=(0,-1,0;1.5708rad)
  LinkedObject = -> <external asm_shf.FCStd>#Hex_socket_head_cap_screw_DIN_912_M4_15_0
  Placement = pos=(12.25,6.5,11.5) rot=(0,-1,0;1.5708rad)
FEATURE [App::Link] Hex_socket_head_cap_screw_DIN_912_M5_15_002  label="Hex socket head cap screw DIN 912 M5 15.002"
  LinkPlacement = pos=(18,11,1.16e-14) rot=(0.57735,-0.57735,0.57735;2.0944rad)
  LinkedObject = -> <external asm_shf.FCStd>#Hex_socket_head_cap_screw_DIN_912_M5_15_0
  Placement = pos=(18,11,1.16e-14) rot=(0.57735,-0.57735,0.57735;2.0944rad)
FEATURE [App::Link] Hex_socket_head_cap_screw_DIN_912_M5_15_003  label="Hex socket head cap screw DIN 912 M5 15.003"
  LinkPlacement = pos=(-18,11,1.16e-14) rot=(0.57735,-0.57735,0.57735;2.0944rad)
  LinkedObject = -> <external asm_shf.FCStd>#Hex_socket_head_cap_screw_DIN_912_M5_15_001
  Placement = pos=(-18,11,1.16e-14) rot=(0.57735,-0.57735,0.57735;2.0944rad)
FEATURE [Assembly::AssemblyLink] asm_SHF001
  Group = -> [SHF013,Hex_socket_head_cap_screw_DIN_912_M4_15_001,Hex_socket_head_cap_screw_DIN_912_M5_15_002,Hex_socket_head_cap_screw_DIN_912_M5_15_003]
  LinkedObject = -> <external asm_shf.FCStd>#Assembly
  Origin = -> Origin002
  Placement = pos=(0,-38,3) rot=(1,0,0;1.5708rad)
  Rigid = true
FEATURE [App::Link] Raspberry_Pi_4_Model_B  label="Raspberry Pi 4 Model B"
  LinkPlacement = pos=(0,8.25,-5.85) rot=(1,0,0;1.5708rad)
  LinkedObject = -> <external asm_rpi.FCStd>#Raspberry_Pi_4_Model_B
  Placement = pos=(0,8.25,-5.85) rot=(1,0,0;1.5708rad)
FEATURE [App::Link] Hex_screw_M2_5_04_0  label="Hex screw M2.5 04.0"
  LinkPlacement = pos=(54.5575,25.7632,-2.56) rot=(-0.707107,0.707107,0;3.14159rad)
  LinkedObject = -> <external asm_rpi.FCStd>#Hex_screw_M2_5_04_0
  Placement = pos=(54.5575,25.7632,-2.56) rot=(-0.707107,0.707107,0;3.14159rad)
FEATURE [App::Link] Hex_screw_M2_5_04_001  label="Hex screw M2.5 04.001"
  LinkPlacement = pos=(-3.44249,-23.2368,-2.56001) rot=(-0.707107,0.707107,0;3.14159rad)
  LinkedObject = -> <external asm_rpi.FCStd>#Hex_screw_M2_5_04_001
  Placement = pos=(-3.44249,-23.2368,-2.56001) rot=(-0.707107,0.707107,0;3.14159rad)
FEATURE [App::Link] Hex_screw_M2_5_04_002  label="Hex screw M2.5 04.002"
  LinkPlacement = pos=(-3.44249,25.7632,-2.56) rot=(-0.707107,0.707107,0;3.14159rad)
  LinkedObject = -> <external asm_rpi.FCStd>#Hex_screw_M2_5_04_002
  Placement = pos=(-3.44249,25.7632,-2.56) rot=(-0.707107,0.707107,0;3.14159rad)
FEATURE [App::Link] Hex_screw_M2_5_04_003  label="Hex screw M2.5 04.003"
  LinkPlacement = pos=(54.5575,-23.2368,-2.56001) rot=(-0.707107,0.707107,0;3.14159rad)
  LinkedObject = -> <external asm_rpi.FCStd>#Hex_screw_M2_5_04_003
  Placement = pos=(54.5575,-23.2368,-2.56001) rot=(-0.707107,0.707107,0;3.14159rad)
FEATURE [Assembly::AssemblyLink] asm_rpi
  Group = -> [Raspberry_Pi_4_Model_B,Hex_screw_M2_5_04_0,Hex_screw_M2_5_04_001,Hex_screw_M2_5_04_002,Hex_screw_M2_5_04_003]
  LinkedObject = -> <external asm_rpi.FCStd>#Assembly
  Origin = -> Origin003
  Placement = pos=(-63.8,10.25,9.64) rot=(0,0,1;3.14159rad)
  Rigid = true
FEATURE [App::Link] cam_holder_base
  LinkPlacement = pos=(0,0,0) rot=(1,0,0;3.14159rad)
  LinkedObject = -> <external asm_cam_mount.FCStd>#cam_holder_base
  Placement = pos=(0,0,0) rot=(1,0,0;3.14159rad)
FEATURE [App::Link] Raspberry_Pi_HQ_Camera_with_cs_mount_lens_v014  label="Raspberry Pi HQ Camera with cs mount lens v014"
  LinkPlacement = pos=(-18.96,19,-3.8) rot=(1,0,0;1.5708rad)
  LinkedObject = -> <external asm_cam_mount.FCStd>#Raspberry_Pi_HQ_Camera_with_cs_mount_lens_v014
  Placement = pos=(-18.96,19,-3.8) rot=(1,0,0;1.5708rad)
FEATURE [App::Link] Hex_screw_M2_5_04_004  label="Hex screw M2.5 04.004"
  LinkPlacement = pos=(-7.97317,-20.5575,-6.3) rot=(0,0,1;0rad)
  LinkedObject = -> <external asm_cam_mount.FCStd>#Hex_screw_M2_5_04_0
  Placement = pos=(-7.97317,-20.5575,-6.3) rot=(0,0,1;0rad)
FEATURE [App::Link] Hex_screw_M2_5_04_005  label="Hex screw M2.5 04.005"
  LinkPlacement = pos=(22.0268,-20.5575,-6.3) rot=(0,0,1;0rad)
  LinkedObject = -> <external asm_cam_mount.FCStd>#Hex_screw_M2_5_04_001
  Placement = pos=(22.0268,-20.5575,-6.3) rot=(0,0,1;0rad)
FEATURE [App::Link] Hex_screw_M2_5_04_006  label="Hex screw M2.5 04.006"
  LinkPlacement = pos=(22.0268,-50.5575,-6.3) rot=(0,0,1;0rad)
  LinkedObject = -> <external asm_cam_mount.FCStd>#Hex_screw_M2_5_04_002
  Placement = pos=(22.0268,-50.5575,-6.3) rot=(0,0,1;0rad)
FEATURE [App::Link] Hex_screw_M2_5_04_007  label="Hex screw M2.5 04.007"
  LinkPlacement = pos=(-7.97317,-50.5575,-6.3) rot=(0,0,1;0rad)
  LinkedObject = -> <external asm_cam_mount.FCStd>#Hex_screw_M2_5_04_003
  Placement = pos=(-7.97317,-50.5575,-6.3) rot=(0,0,1;0rad)
FEATURE [App::Link] Hex_screw_M4_10_0  label="Hex screw M4 10.0"
  LinkPlacement = pos=(-25.9732,-58.0575,-20.5) rot=(0,0,1;0rad)
  LinkedObject = -> <external asm_cam_mount.FCStd>#Hex_screw_M4_10_0
  Placement = pos=(-25.9732,-58.0575,-20.5) rot=(0,0,1;0rad)
FEATURE [App::Link] Hex_screw_M4_10_001  label="Hex screw M4 10.001"
  LinkPlacement = pos=(-25.9732,-20.0575,-20.5) rot=(0,0,1;0rad)
  LinkedObject = -> <external asm_cam_mount.FCStd>#Hex_screw_M4_10_001
  Placement = pos=(-25.9732,-20.0575,-20.5) rot=(0,0,1;0rad)
FEATURE [App::Link] Hex_screw_M4_10_002  label="Hex screw M4 10.002"
  LinkPlacement = pos=(39.9468,-58.0575,-20.5) rot=(0,0,1;0rad)
  LinkedObject = -> <external asm_cam_mount.FCStd>#Hex_screw_M4_10_002
  Placement = pos=(39.9468,-58.0575,-20.5) rot=(0,0,1;0rad)
FEATURE [App::Link] Hex_screw_M4_10_003  label="Hex screw M4 10.003"
  LinkPlacement = pos=(39.9468,-20.0575,-20.5) rot=(0,0,1;0rad)
  LinkedObject = -> <external asm_cam_mount.FCStd>#Hex_screw_M4_10_003
  Placement = pos=(39.9468,-20.0575,-20.5) rot=(0,0,1;0rad)
FEATURE [Assembly::AssemblyLink] asm_cam_mount
  Group = -> [cam_holder_base,Raspberry_Pi_HQ_Camera_with_cs_mount_lens_v014,Hex_screw_M2_5_04_004,Hex_screw_M2_5_04_005,Hex_screw_M2_5_04_006,Hex_screw_M2_5_04_007,Hex_screw_M4_10_0,Hex_screw_M4_10_001,Hex_screw_M4_10_002,Hex_screw_M4_10_003]
  LinkedObject = -> <external asm_cam_mount.FCStd>#Assembly
  Origin = -> Origin004
  Placement = pos=(58.5311,-2.9e-15,15.5) rot=(0,0,1;4.71239rad)
  Rigid = true
FEATURE [App::FeaturePython] Joint  label="Fixed"  # Assembly joint (typed FeaturePython)
  Activated = true
  AngleMax = 0
  AngleMin = 0
  Detach1 = false
  Detach2 = false
  Distance = 0
  Distance2 = 0
  EnableAngleMax = false
  EnableAngleMin = false
  EnableLengthMax = false
  EnableLengthMin = false
  JointType = 0 (Fixed)
  LengthMax = 0
  LengthMin = 0
  Offset2 = pos=(0,0,0) rot=(0,0,1;1.5708rad)
  Placement1 = pos=(19,-0.79,24.5) rot=(0.57735,0.57735,0.57735;4.18879rad)
  Placement2 = pos=(-82.8,26.5,3) rot=(0,0,1;1.5708rad)
  Reference1 = -> Assembly [asm_rpi.Raspberry_Pi_4_Model_B.Part__Feature.Edge337,asm_rpi.Raspberry_Pi_4_Model_B.Part__Feature.Edge337]
  Reference2 = -> Assembly [cam_holder_plate.Edge66,cam_holder_plate.Edge66]
FEATURE [App::FeaturePython] Joint001  label="Fixed001"  # Assembly joint (typed FeaturePython)
  Activated = true
  AngleMax = 0
  AngleMin = 0
  Detach1 = false
  Detach2 = false
  Distance = 0
  Distance2 = 0
  EnableAngleMax = false
  EnableAngleMin = false
  EnableLengthMax = false
  EnableLengthMin = false
  JointType = 0 (Fixed)
  LengthMax = 0
  LengthMin = 0
  Offset2 = pos=(0,0,0) rot=(0,0,-1;1.5708rad)
  Placement1 = pos=(18,0,1.16e-14) rot=(-0.57735,0.57735,0.57735;2.0944rad)
  Placement2 = pos=(-18,38,3) rot=(0,0,-1;1.5708rad)
  Reference1 = -> Assembly [asm_SHF.SHF12.Edge109,asm_SHF.SHF12.Edge109]
  Reference2 = -> Assembly [cam_holder_plate.Edge45,cam_holder_plate.Edge45]
FEATURE [App::FeaturePython] Joint002  label="Fixed002"  # Assembly joint (typed FeaturePython)
  Activated = true
  AngleMax = 0
  AngleMin = 0
  Detach1 = false
  Detach2 = false
  Distance = 0
  Distance2 = 0
  EnableAngleMax = false
  EnableAngleMin = false
  EnableLengthMax = false
  EnableLengthMin = false
  JointType = 0 (Fixed)
  LengthMax = 0
  LengthMin = 0
  Offset2 = pos=(0,0,0) rot=(0,0,-1;1.5708rad)
  Placement1 = pos=(-18,0,1.16e-14) rot=(0.57735,0.57735,0.57735;4.18879rad)
  Placement2 = pos=(-18,-38,3) rot=(0,0,-1;1.5708rad)
  Reference1 = -> Assembly [asm_SHF001.SHF013.Edge27,asm_SHF001.SHF013.Edge27]
  Reference2 = -> Assembly [cam_holder_plate.Edge51,cam_holder_plate.Edge51]
FEATURE [App::FeaturePython] Joint003  label="Fixed003"  # Assembly joint (typed FeaturePython)
  Activated = true
  AngleMax = 0
  AngleMin = 0
  Detach1 = false
  Detach2 = false
  Distance = 0
  Distance2 = 0
  EnableAngleMax = false
  EnableAngleMin = false
  EnableLengthMax = false
  EnableLengthMin = false
  JointType = 0 (Fixed)
  LengthMax = 0
  LengthMin = 0
  Offset2 = pos=(0,0,0) rot=(0,0,-1;1.5708rad)
  Placement1 = pos=(32.96,22.5,12.5) rot=(0,0,1;0rad)
  Placement2 = pos=(36.0311,-32.96,3) rot=(0,0,-1;1.5708rad)
  Reference1 = -> Assembly [asm_cam_mount.cam_holder_base.Edge111,asm_cam_mount.cam_holder_base.Edge111]
  Reference2 = -> Assembly [cam_holder_plate.Edge39,cam_holder_plate.Edge39]
FEATURE [Assembly::JointGroup] Joints
  Group = -> [GroundedJoint,Joint,Joint001,Joint002,Joint003]
FEATURE [Assembly::AssemblyObject] Assembly  label="asm_cam_holder"
  Group = -> [Joints,cam_holder_plate,GroundedJoint,asm_SHF,asm_SHF001,asm_rpi,asm_cam_mount,Joint,Joint001,Joint002,Joint003]
  Origin = -> Origin
  Type = Assembly
---- part asm_shf.FCStd = doc fcstd_04160f494026 ----
FCSTD DOCUMENT  (FreeCAD 1.0R39109 (Git))
Label: asm_shf
License: All rights reserved
LicenseURL: https://en.wikipedia.org/wiki/All_rights_reserved
objects: App::Link×4, App::FeaturePython×3, Assembly::JointGroup×1, Assembly::AssemblyObject×1
EXTERNAL_REF file=../downloads/linear-bearing-shaft-support-shf12-1.snapshot.1/SHF_12.FCStd obj=Part__Feature
EXTERNAL_REF file=../secondary/bolts.FCStd obj=BOLTS_part001
EXTERNAL_REF file=../secondary/bolts.FCStd obj=BOLTS_part004

FEATURE [App::Link] SHF12
  LinkedObject = -> <external ../downloads/linear-bearing-shaft-support-shf12-1.snapshot.1/SHF_12.FCStd>#Part__Feature
FEATURE [App::FeaturePython] GroundedJoint  # Assembly grounded joint (typed FeaturePython)
  ObjectToGround = -> SHF12
FEATURE [App::Link] Hex_socket_head_cap_screw_DIN_912_M4_15_0  label="Hex socket head cap screw DIN 912 M4 15.0"
  LinkPlacement = pos=(12.25,6.5,11.5) rot=(0,-1,0;1.5708rad)
  LinkedObject = -> <external ../secondary/bolts.FCStd>#BOLTS_part001
  Placement = pos=(12.25,6.5,11.5) rot=(0,-1,0;1.5708rad)
FEATURE [App::Link] Hex_socket_head_cap_screw_DIN_912_M5_15_0  label="Hex socket head cap screw DIN 912 M5 15.0"
  LinkPlacement = pos=(18,11,1.16e-14) rot=(0.57735,-0.57735,0.57735;2.0944rad)
  LinkedObject = -> <external ../secondary/bolts.FCStd>#BOLTS_part004
  Placement = pos=(18,11,1.16e-14) rot=(0.57735,-0.57735,0.57735;2.0944rad)
FEATURE [App::Link] Hex_socket_head_cap_screw_DIN_912_M5_15_001  label="Hex socket head cap screw DIN 912 M5 15.001"
  LinkPlacement = pos=(-18,11,1.16e-14) rot=(0.57735,-0.57735,0.57735;2.0944rad)
  LinkedObject = -> <external ../secondary/bolts.FCStd>#BOLTS_part004
  Placement = pos=(-18,11,1.16e-14) rot=(0.57735,-0.57735,0.57735;2.0944rad)
FEATURE [App::FeaturePython] Joint001  label="Fixed001"  # Assembly joint (typed FeaturePython)
  Activated = true
  AngleMax = 0
  AngleMin = 0
  Detach1 = false
  Detach2 = false
  Distance = 0
  Distance2 = 0
  EnableAngleMax = false
  EnableAngleMin = false
  EnableLengthMax = false
  EnableLengthMin = false
  JointType = 0 (Fixed)
  LengthMax = 0
  LengthMin = 0
  Placement1 = pos=(-18,6,1.16e-14) rot=(0.57735,0.57735,0.57735;4.18879rad)
  Placement2 = pos=(-6e-16,-3.6e-15,5) rot=(0,0,1;0rad)
  Reference1 = -> Assembly [SHF12.Edge68,SHF12.Edge68]
  Reference2 = -> Assembly [Hex_socket_head_cap_screw_DIN_912_M5_15_001.Edge4,Hex_socket_head_cap_screw_DIN_912_M5_15_001.Edge4]
FEATURE [App::FeaturePython] Joint002  label="Fixed002"  # Assembly joint (typed FeaturePython)
  Activated = true
  AngleMax = 0
  AngleMin = 0
  Detach1 = false
  Detach2 = false
  Distance = 0
  Distance2 = 0
  EnableAngleMax = false
  EnableAngleMin = false
  EnableLengthMax = false
  EnableLengthMin = false
  JointType = 0 (Fixed)
  LengthMax = 0
  LengthMin = 0
FEATURE [Assembly::JointGroup] Joints
  Group = -> [GroundedJoint,Joint001,Joint002]
FEATURE [Assembly::AssemblyObject] Assembly  label="asm_SHF"
  Group = -> [Joints,SHF12,GroundedJoint,Hex_socket_head_cap_screw_DIN_912_M4_15_0,Hex_socket_head_cap_screw_DIN_912_M5_15_0,Hex_socket_head_cap_screw_DIN_912_M5_15_001,Joint001,Joint002]
  Origin = -> Origin
  Type = Assembly
